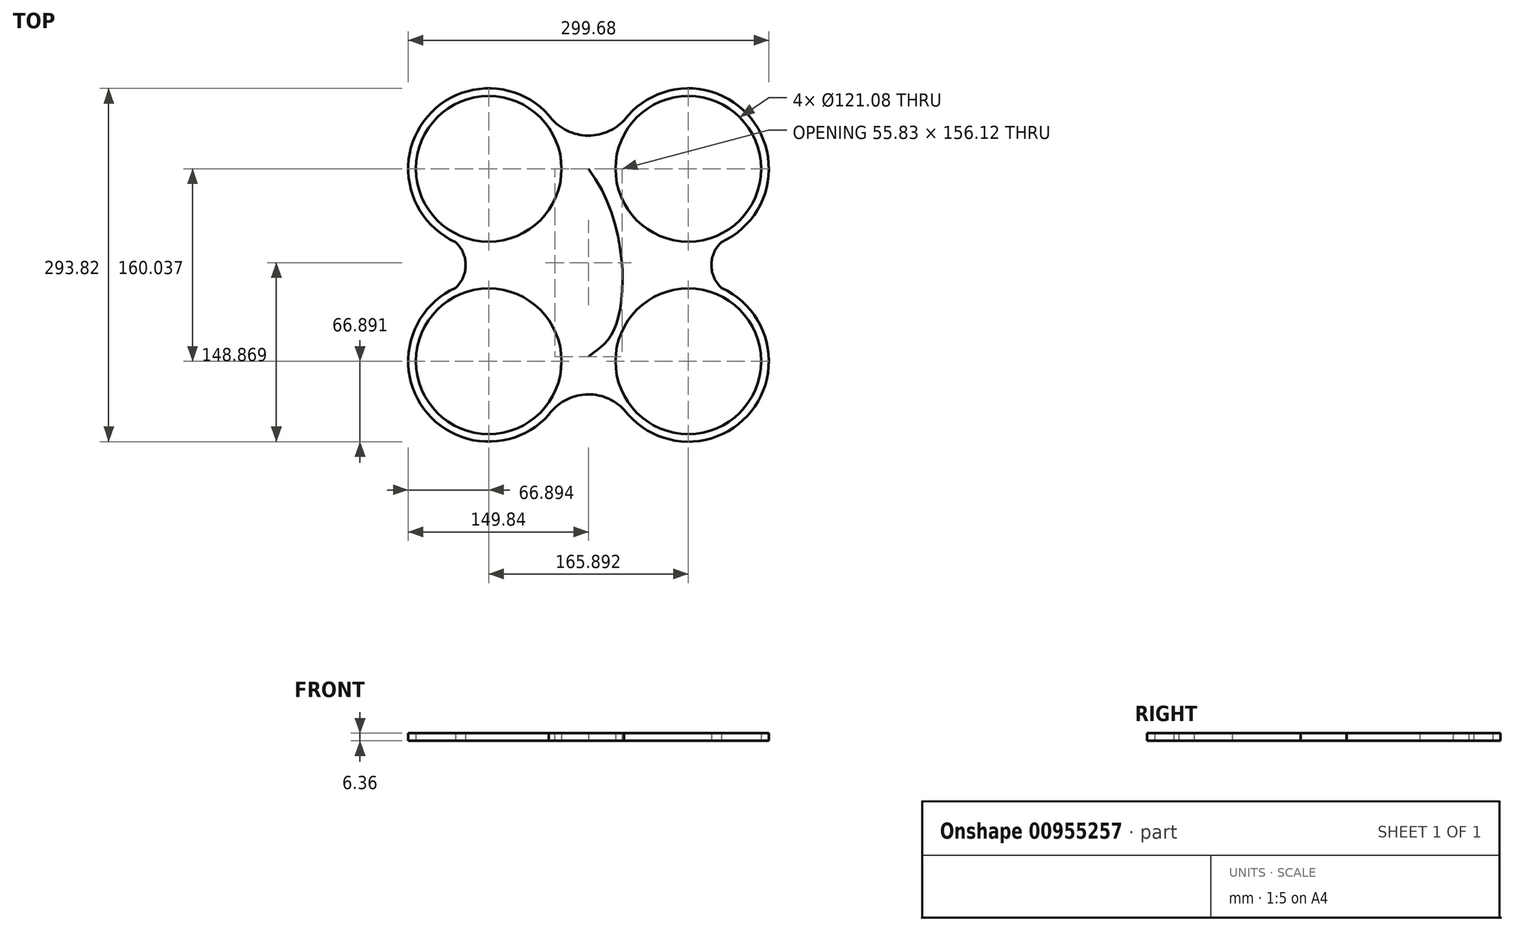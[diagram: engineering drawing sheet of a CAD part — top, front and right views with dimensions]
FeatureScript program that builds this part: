
annotation { "Feature Type Name" : "Feature", "Feature Type Description" : "" }
export const myFeature = defineFeature(function(context is Context, id is Id, definition is map)
    precondition{}
    {
        {
            var Q0;
            Q0=qCreatedBy(makeId("Top.planeOp"),FACE);
            var sketch = newSketch(context, id + "F0", { "sketchPlane" : qUnion([Q0])});
            skFitSpline(sketch, "E0", {"points": [v(0, -76.1) * mm, v(-22.63, -50.46) * mm, v(0, 80.02) * mm], "startDerivative": vector(-85.28, 61.38) * mm, "endDerivative": vector(144.03, 192.46) * mm});
            skArc(sketch, "E1", {"start": v(-29.64, 120.43) * mm, "mid": v(-135.2, 121.77) * mm, "end": v(-110.58, 19.1) * mm});
            skArc(sketch, "E2.MirrorC", {"start": v(-29.64, -120.43) * mm, "mid": v(-135.2, -121.77) * mm, "end": v(-110.58, -19.1) * mm});
            skArc(sketch, "E3.MirrorC", {"start": v(29.64, 120.43) * mm, "mid": v(135.2, 121.77) * mm, "end": v(110.58, 19.1) * mm});
            skArc(sketch, "E4.MirrorC", {"start": v(29.64, -120.43) * mm, "mid": v(135.2, -121.77) * mm, "end": v(110.58, -19.1) * mm});
            skFitSpline(sketch, "E5.MirrorCS", {"points": [v(0, -76.1) * mm, v(22.63, -50.46) * mm, v(0, 80.02) * mm], "startDerivative": vector(85.28, 61.38) * mm, "endDerivative": vector(-144.03, 192.46) * mm});
            skArc(sketch, "E6", {"start": v(-110.58, 19.1) * mm, "mid": v(-102.11, 0) * mm, "end": v(-110.58, -19.1) * mm});
            skArc(sketch, "E7.MirrorCS", {"start": v(110.58, 19.1) * mm, "mid": v(102.11, 0) * mm, "end": v(110.58, -19.1) * mm});
            skArc(sketch, "E8", {"start": v(-33.03, 124.55) * mm, "mid": v(-2.67, 107.7) * mm, "end": v(29.64, 120.43) * mm});
            skArc(sketch, "E9.MirrorCS", {"start": v(-33.03, -124.55) * mm, "mid": v(-2.67, -107.7) * mm, "end": v(29.64, -120.43) * mm});
            skPoint(sketch, "E10.MirrorCS.start.orphan", {"position": v(0, 0) * mm});
            skLineSegment(sketch, "E11", {"start": v(0, -76.1) * mm, "end": v(0, 0) * mm});
            skCircle(sketch, "E12.0", {"center": v(-82.95, -80.02) * mm, "radius": 60.54 * mm});
            skCircle(sketch, "E13.0", {"center": v(-82.95, 80.02) * mm, "radius": 5.6 * mm});
            skCircle(sketch, "E14.MirrorC", {"center": v(82.95, -80.02) * mm, "radius": 60.54 * mm});
            skCircle(sketch, "E15.MirrorC", {"center": v(-82.95, 80.02) * mm, "radius": 60.54 * mm});
            skCircle(sketch, "E16.MirrorC", {"center": v(82.95, 80.02) * mm, "radius": 60.54 * mm});
            skSolve(sketch);
        }
        {
            var Q0;
            Q0 = qSketchRegion(id + "F0", true);
            var Q1;
            Q1=sQuery(id+"F0.wireOp",EDGE,"E5.MirrorCS");
            var Q2;
            Q2=sQuery(id+"F0.wireOp",EDGE,"E11");
            revolve(context, id + "F1", {"bodyType" : ToolBodyType.SURFACE, "surfaceOperationType" : NewSurfaceOperationType.NEW, "entities" : qUnion([Q0]), "surfaceEntities" : qUnion([Q1]), "axis" : qUnion([Q2]), "revolveType" : RevolveType.ONE_DIRECTION, "angle" : 180 * degree});
        }
        {
            var Q0;
            Q0=makeQuery(id+"F0.imprint","IMPRINT",FACE,{"disambiguationData":[TD([[makeQuery(id+"F0.imprint","IMPRINT",EDGE,{"derivedFrom":sQuery(id+"F0.wireOp",EDGE,"E0")}),1.0]])]});
            extrude(context, id + "F2", {"entities" : qUnion([Q0]), "endBound" : BoundingType.SYMMETRIC, "depth" : 6.35 * mm, "offsetDistance" : 25.4 * mm});
        }
        {
            var Q0;
            Q0 = qSketchRegion(id + "F0", true);
            var Q1;
            Q1=sQuery(id+"F0.wireOp",EDGE,"E5.MirrorCS");
            var Q2;
            Q2=sQuery(id+"F0.wireOp",EDGE,"E11");
            revolve(context, id + "F3", {"bodyType" : ToolBodyType.SURFACE, "surfaceOperationType" : NewSurfaceOperationType.NEW, "entities" : qUnion([Q0]), "surfaceEntities" : qUnion([Q1]), "axis" : qUnion([Q2]), "revolveType" : RevolveType.ONE_DIRECTION, "oppositeDirection" : true, "angle" : 180 * degree});
        }
    });
